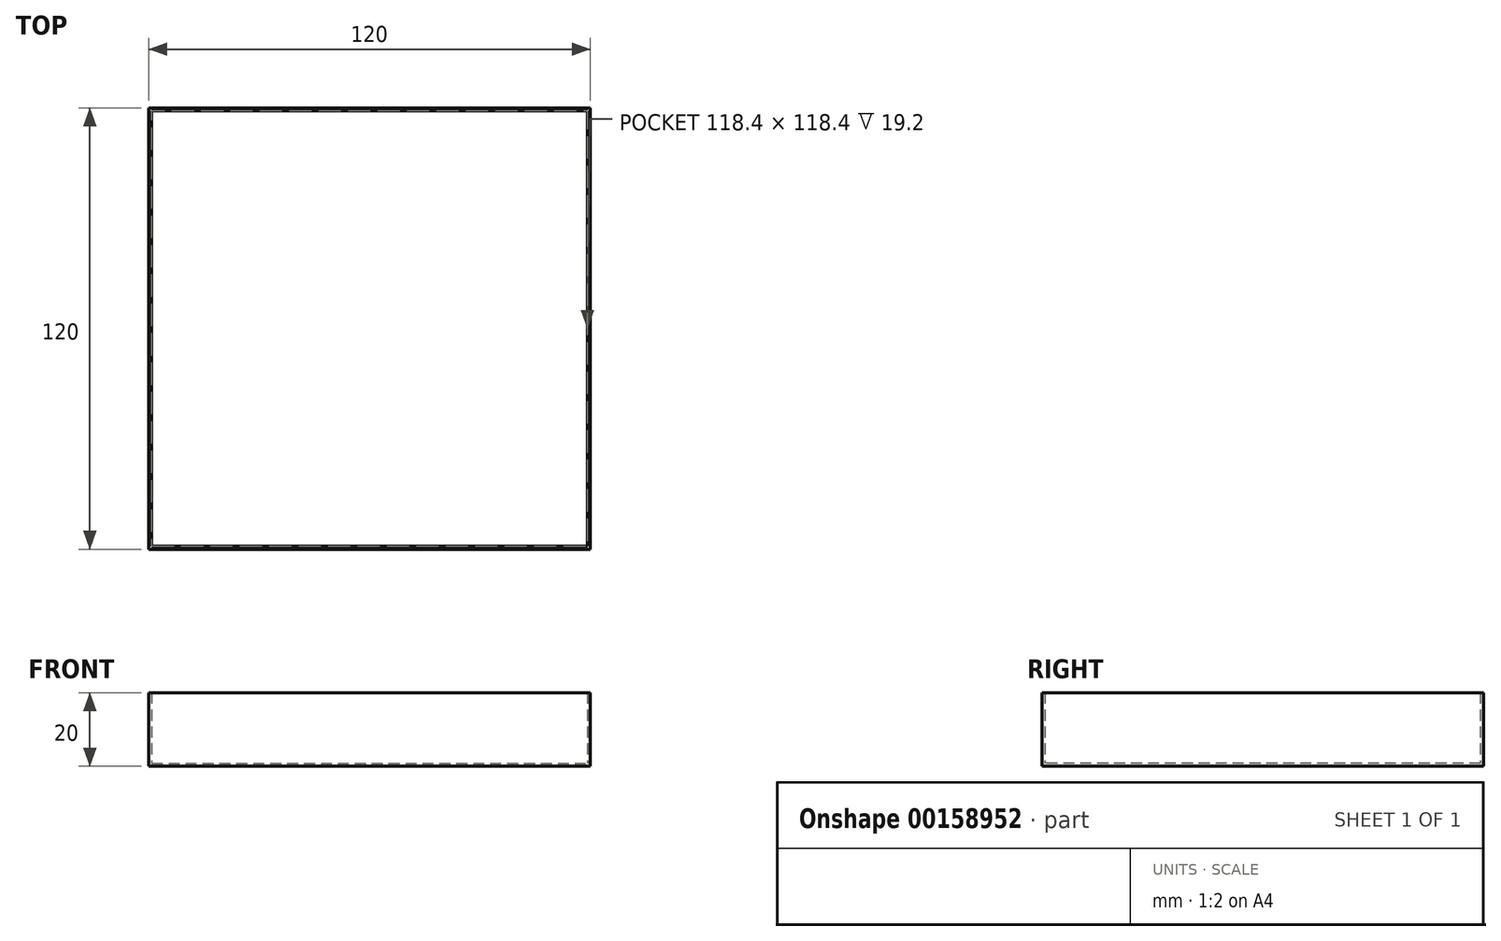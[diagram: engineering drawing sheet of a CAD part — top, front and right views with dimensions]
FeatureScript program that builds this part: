
annotation { "Feature Type Name" : "Feature", "Feature Type Description" : "" }
export const myFeature = defineFeature(function(context is Context, id is Id, definition is map)
    precondition{}
    {
        {
            var Q0;
            Q0=qCreatedBy(makeId("Top.planeOp"),FACE);
            var sketch = newSketch(context, id + "F0", { "sketchPlane" : qUnion([Q0])});
            skLineSegment(sketch, "E0.bottom", {"start": v(-60, 60) * mm, "end": v(60, 60) * mm});
            skLineSegment(sketch, "E0.top", {"start": v(-60, -60) * mm, "end": v(60, -60) * mm});
            skLineSegment(sketch, "E0.left", {"start": v(-60, 60) * mm, "end": v(-60, -60) * mm});
            skLineSegment(sketch, "E0.right", {"start": v(60, 60) * mm, "end": v(60, -60) * mm});
            skLineSegment(sketch, "E1", {"start": v(0, 60) * mm, "end": v(0, 0) * mm, "construction": true});
            skLineSegment(sketch, "E2", {"start": v(0, 0) * mm, "end": v(0, -60) * mm, "construction": true});
            skLineSegment(sketch, "E3", {"start": v(0, 0) * mm, "end": v(60, 0) * mm, "construction": true});
            skLineSegment(sketch, "E4", {"start": v(0, 0) * mm, "end": v(-60, 0) * mm, "construction": true});
            skSolve(sketch);
        }
        {
            var Q0;
            Q0 = qSketchRegion(id + "F0", true);
            extrude(context, id + "F1", {"entities" : qUnion([Q0]), "depth" : 20 * mm});
        }
        {
            var Q0;
            Q0=makeQuery(id+"F1.opExtrude","CAP_FACE",FACE,{"disambiguationData":[OSD([sQuery(id+"F0.wireOp",EDGE,"E0.bottom"),sQuery(id+"F0.wireOp",EDGE,"E0.top"),sQuery(id+"F0.wireOp",EDGE,"E0.left"),sQuery(id+"F0.wireOp",EDGE,"E0.right")])],"isStart":false});
            shell(context, id + "F2", {"entities" : qUnion([Q0]), "thickness" : 0.8 * mm});
        }
    });
